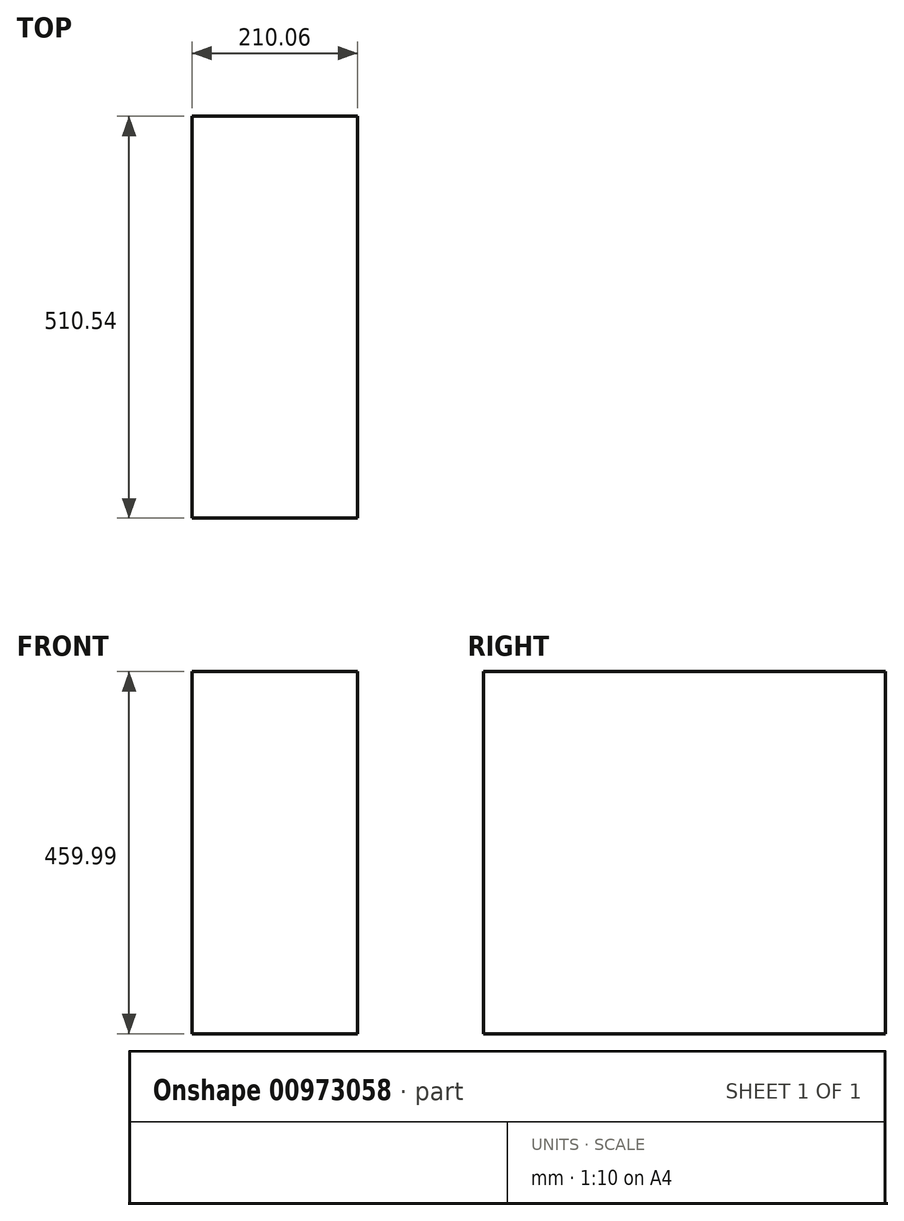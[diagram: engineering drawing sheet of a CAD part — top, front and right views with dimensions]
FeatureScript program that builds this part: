
annotation { "Feature Type Name" : "Feature", "Feature Type Description" : "" }
export const myFeature = defineFeature(function(context is Context, id is Id, definition is map)
    precondition{}
    {
        {
            var Q0;
            Q0=qCreatedBy(makeId("Top.planeOp"),FACE);
            var sketch = newSketch(context, id + "F0", { "sketchPlane" : qUnion([Q0])});
            skLineSegment(sketch, "E0.bottom", {"start": v(105.03, 255.27) * mm, "end": v(-105.03, 255.27) * mm});
            skLineSegment(sketch, "E0.top", {"start": v(105.03, -255.27) * mm, "end": v(-105.03, -255.27) * mm});
            skLineSegment(sketch, "E0.left", {"start": v(105.03, 255.27) * mm, "end": v(105.03, -255.27) * mm});
            skLineSegment(sketch, "E0.right", {"start": v(-105.03, 255.27) * mm, "end": v(-105.03, -255.27) * mm});
            skPoint(sketch, "E0.middle", {"position": v(0, 0) * mm});
            skSolve(sketch);
        }
        {
            var Q0;
            Q0 = qSketchRegion(id + "F0", true);
            extrude(context, id + "F1", {"entities" : qUnion([Q0]), "depth" : 460 * mm, "offsetDistance" : 25.4 * mm});
        }
    });
